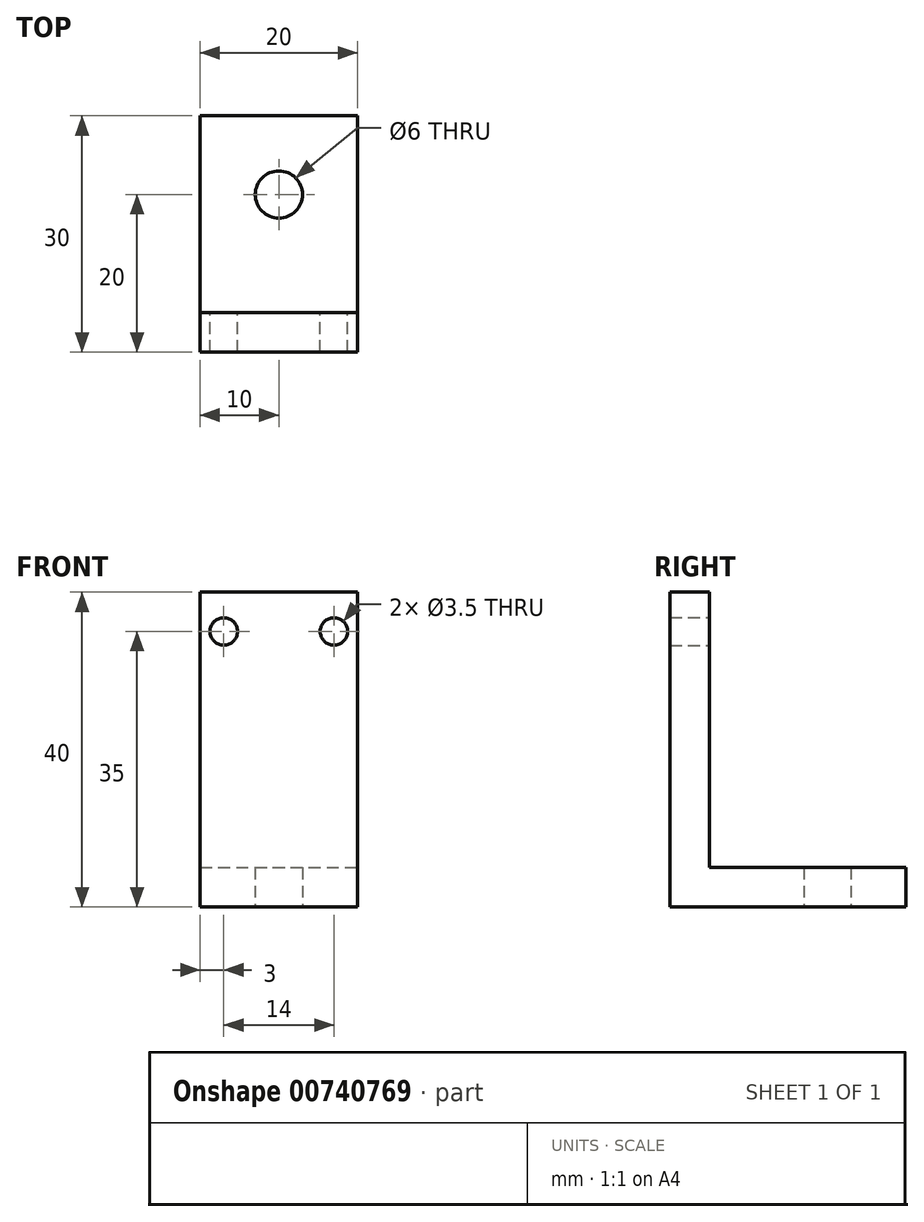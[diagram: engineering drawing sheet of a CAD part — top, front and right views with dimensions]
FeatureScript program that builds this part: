
annotation { "Feature Type Name" : "Feature", "Feature Type Description" : "" }
export const myFeature = defineFeature(function(context is Context, id is Id, definition is map)
    precondition{}
    {
        {
            var Q0;
            Q0=qCreatedBy(makeId("Front.planeOp"),FACE);
            var sketch = newSketch(context, id + "F0", { "sketchPlane" : qUnion([Q0])});
            skLineSegment(sketch, "E0.bottom", {"start": v(-10, 20) * mm, "end": v(10, 20) * mm});
            skLineSegment(sketch, "E0.top", {"start": v(-10, -20) * mm, "end": v(10, -20) * mm});
            skLineSegment(sketch, "E0.left", {"start": v(-10, 20) * mm, "end": v(-10, -20) * mm});
            skLineSegment(sketch, "E0.right", {"start": v(10, 20) * mm, "end": v(10, -20) * mm});
            skPoint(sketch, "E0.middle", {"position": v(0, 0) * mm});
            skCircle(sketch, "E1", {"center": v(-7, 15) * mm, "radius": 1.75 * mm});
            skCircle(sketch, "E2.MirrorC", {"center": v(7, 15) * mm, "radius": 1.75 * mm});
            skSolve(sketch);
        }
        {
            var Q0;
            Q0 = qSketchRegion(id + "F0", true);
            extrude(context, id + "F1", {"entities" : qUnion([Q0]), "depth" : 5 * mm, "offsetDistance" : 25 * mm});
        }
        {
            var Q0;
            Q0=makeQuery(id+"F1.opExtrude","SWEPT_FACE",FACE,{"disambiguationData":[OSD([sQuery(id+"F0.wireOp",EDGE,"E0.top")])]});
            var sketch = newSketch(context, id + "F2", { "sketchPlane" : qUnion([Q0])});
            skLineSegment(sketch, "E3.bottom", {"start": v(-10, 5) * mm, "end": v(10, 5) * mm});
            skLineSegment(sketch, "E3.top", {"start": v(-10, -25) * mm, "end": v(10, -25) * mm});
            skLineSegment(sketch, "E3.left", {"start": v(-10, 5) * mm, "end": v(-10, -25) * mm});
            skLineSegment(sketch, "E3.right", {"start": v(10, 5) * mm, "end": v(10, -25) * mm});
            skCircle(sketch, "E4", {"center": v(0, -15) * mm, "radius": 3 * mm});
            skSolve(sketch);
        }
        {
            var Q0;
            Q0 = qSketchRegion(id + "F2", true);
            extrude(context, id + "F3", {"entities" : qUnion([Q0]), "operationType" : NewBodyOperationType.ADD, "oppositeDirection" : true, "depth" : 5 * mm, "offsetDistance" : 25 * mm});
        }
    });
